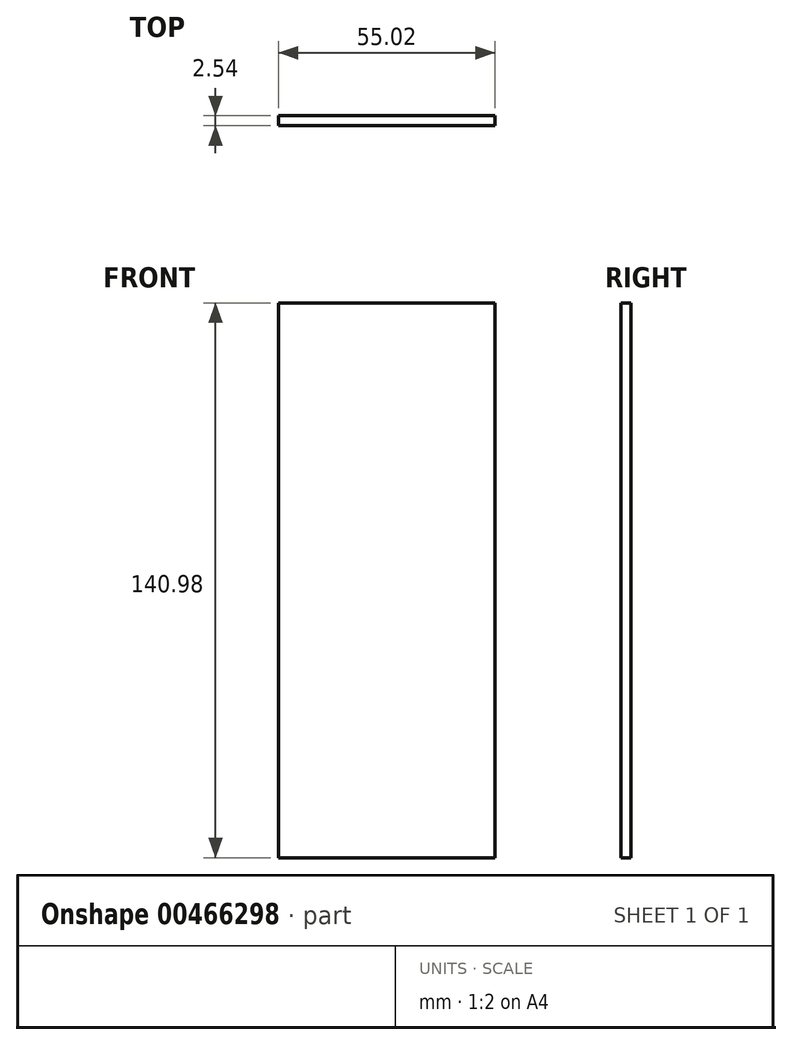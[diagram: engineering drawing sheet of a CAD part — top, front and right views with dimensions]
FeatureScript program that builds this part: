
annotation { "Feature Type Name" : "Feature", "Feature Type Description" : "" }
export const myFeature = defineFeature(function(context is Context, id is Id, definition is map)
    precondition{}
    {
        {
            var Q0;
            Q0=qCreatedBy(makeId("Front.planeOp"),FACE);
            var sketch = newSketch(context, id + "F0", { "sketchPlane" : qUnion([Q0])});
            skLineSegment(sketch, "E0.bottom", {"start": v(-103.6, 67.55) * mm, "end": v(-48.58, 67.55) * mm});
            skLineSegment(sketch, "E0.top", {"start": v(-103.6, -73.43) * mm, "end": v(-48.58, -73.43) * mm});
            skLineSegment(sketch, "E0.left", {"start": v(-103.6, 67.55) * mm, "end": v(-103.6, -73.43) * mm});
            skLineSegment(sketch, "E0.right", {"start": v(-48.58, 67.55) * mm, "end": v(-48.58, -73.43) * mm});
            skSolve(sketch);
        }
        {
            var Q0;
            Q0=makeQuery(id+"F0.imprint","IMPRINT",FACE,{"disambiguationData":[TD([[makeQuery(id+"F0.imprint","IMPRINT",EDGE,{"derivedFrom":sQuery(id+"F0.wireOp",EDGE,"E0.bottom")}),-1.0]])]});
            extrude(context, id + "F1", {"entities" : qUnion([Q0]), "oppositeDirection" : true, "depth" : 2.54 * mm});
        }
    });
